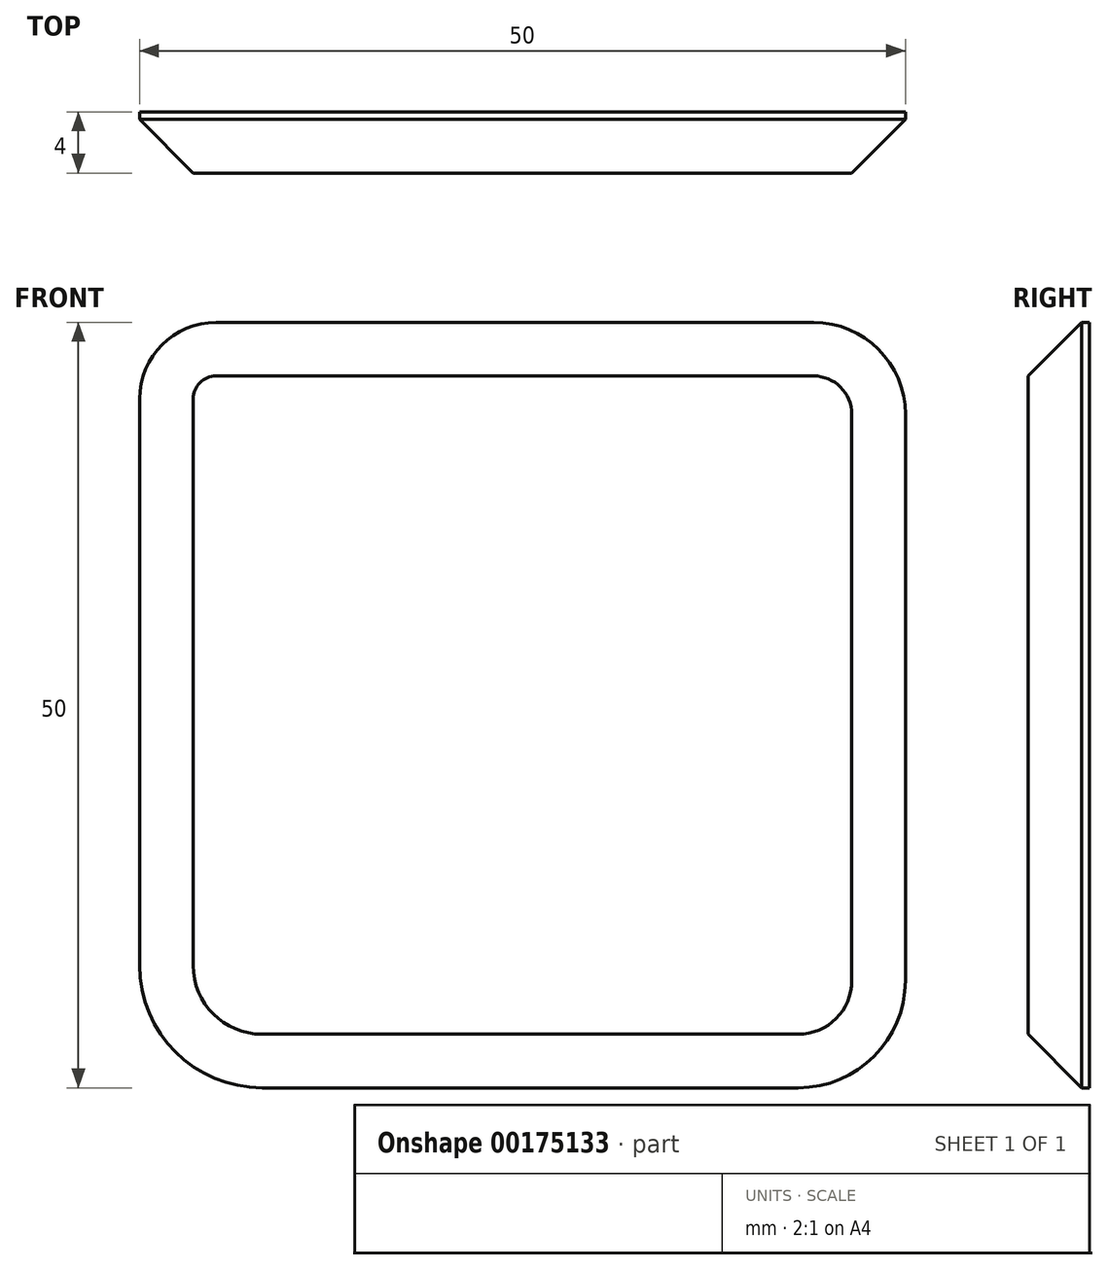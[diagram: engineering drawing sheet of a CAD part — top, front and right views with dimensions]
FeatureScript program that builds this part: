
annotation { "Feature Type Name" : "Feature", "Feature Type Description" : "" }
export const myFeature = defineFeature(function(context is Context, id is Id, definition is map)
    precondition{}
    {
        {
            var Q0;
            Q0=qCreatedBy(makeId("Front.planeOp"),FACE);
            var sketch = newSketch(context, id + "F0", { "sketchPlane" : qUnion([Q0])});
            skLineSegment(sketch, "E0.bottom", {"start": v(19, 25) * mm, "end": v(-20, 25) * mm});
            skLineSegment(sketch, "E0.top", {"start": v(18, -25) * mm, "end": v(-17, -25) * mm});
            skLineSegment(sketch, "E0.left", {"start": v(25, 19) * mm, "end": v(25, -18) * mm});
            skLineSegment(sketch, "E0.right", {"start": v(-25, 20) * mm, "end": v(-25, -17) * mm});
            skPoint(sketch, "E0.middle", {"position": v(0, 0) * mm});
            skPoint(sketch, "E1.visualSharp", {"position": v(-25, 25) * mm});
            skArc(sketch, "E1.filletArc", {"start": v(-20, 25) * mm, "mid": v(-23.54, 23.54) * mm, "end": v(-25, 20) * mm});
            skPoint(sketch, "E2.visualSharp", {"position": v(-25, -25) * mm});
            skArc(sketch, "E2.filletArc", {"start": v(-25, -17) * mm, "mid": v(-22.66, -22.66) * mm, "end": v(-17, -25) * mm});
            skPoint(sketch, "E3.visualSharp", {"position": v(25, 25) * mm});
            skArc(sketch, "E3.filletArc", {"start": v(25, 19) * mm, "mid": v(23.24, 23.24) * mm, "end": v(19, 25) * mm});
            skPoint(sketch, "E4.visualSharp", {"position": v(25, -25) * mm});
            skArc(sketch, "E4.filletArc", {"start": v(18, -25) * mm, "mid": v(22.95, -22.95) * mm, "end": v(25, -18) * mm});
            skSolve(sketch);
        }
        {
            var Q0;
            Q0=makeQuery(id+"F0.imprint","IMPRINT",FACE,{"disambiguationData":[TD([[makeQuery(id+"F0.imprint","IMPRINT",EDGE,{"derivedFrom":sQuery(id+"F0.wireOp",EDGE,"E0.bottom")}),1.0]])]});
            extrude(context, id + "F1", {"entities" : qUnion([Q0]), "depth" : 4 * mm});
        }
        {
            var Q0;
            Q0=makeQuery(id+"F1.opExtrude","CAP_FACE",FACE,{"disambiguationData":[OSD([sQuery(id+"F0.wireOp",EDGE,"E0.bottom"),sQuery(id+"F0.wireOp",EDGE,"E0.top"),sQuery(id+"F0.wireOp",EDGE,"E0.left"),sQuery(id+"F0.wireOp",EDGE,"E0.right"),sQuery(id+"F0.wireOp",EDGE,"E1.filletArc"),sQuery(id+"F0.wireOp",EDGE,"E2.filletArc"),sQuery(id+"F0.wireOp",EDGE,"E3.filletArc"),sQuery(id+"F0.wireOp",EDGE,"E4.filletArc")])],"isStart":false});
            chamfer(context, id + "F2", {"entities" : qUnion([Q0]), "width" : 3.5 * mm, "tangentPropagation" : true});
        }
    });
